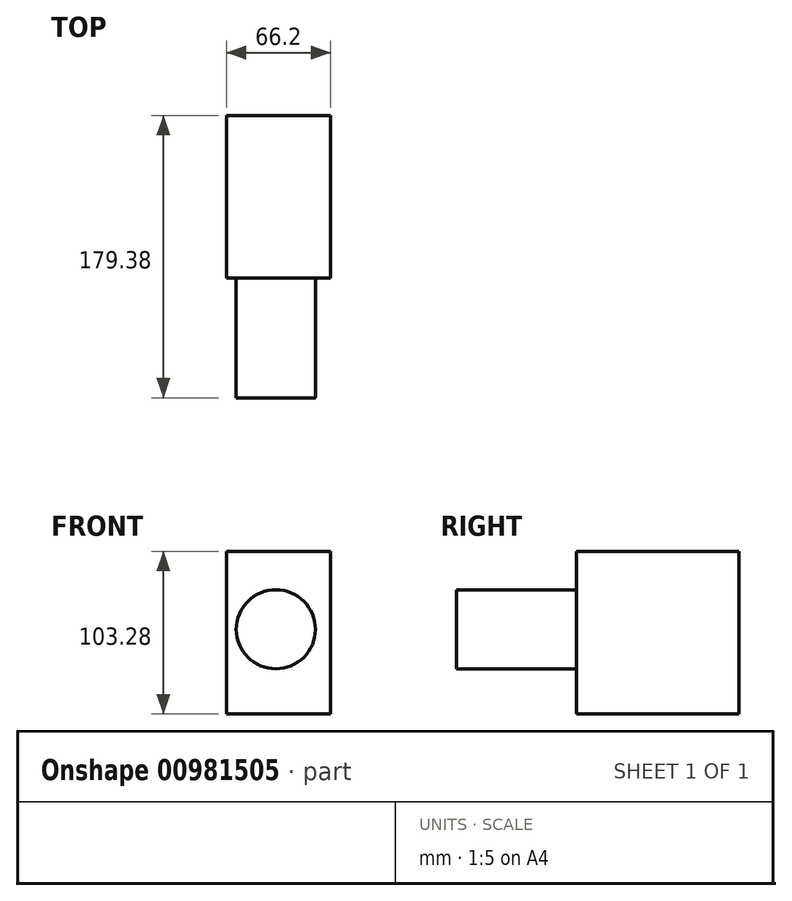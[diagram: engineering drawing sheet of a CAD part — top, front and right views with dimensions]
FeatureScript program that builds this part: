
annotation { "Feature Type Name" : "Feature", "Feature Type Description" : "" }
export const myFeature = defineFeature(function(context is Context, id is Id, definition is map)
    precondition{}
    {
        {
            var Q0;
            Q0=qCreatedBy(makeId("Top.planeOp"),FACE);
            var sketch = newSketch(context, id + "F0", { "sketchPlane" : qUnion([Q0])});
            skLineSegment(sketch, "E0.bottom", {"start": v(17.44, -38.98) * mm, "end": v(-48.76, -38.98) * mm});
            skLineSegment(sketch, "E0.top", {"start": v(17.44, 64.3) * mm, "end": v(-48.76, 64.3) * mm});
            skLineSegment(sketch, "E0.left", {"start": v(17.44, -38.98) * mm, "end": v(17.44, 64.3) * mm});
            skLineSegment(sketch, "E0.right", {"start": v(-48.76, -38.98) * mm, "end": v(-48.76, 64.3) * mm});
            skSolve(sketch);
        }
        {
            var Q0;
            Q0=makeQuery(id+"F0.imprint","IMPRINT",FACE,{"disambiguationData":[TD([[makeQuery(id+"F0.imprint","IMPRINT",EDGE,{"derivedFrom":sQuery(id+"F0.wireOp",EDGE,"E0.bottom")}),-1.0]])]});
            extrude(context, id + "F1", {"entities" : qUnion([Q0]), "depth" : 103.28 * mm, "offsetDistance" : 25.4 * mm});
        }
        {
            var Q0;
            Q0=makeQuery(id+"F1.opExtrude","SWEPT_FACE",FACE,{"disambiguationData":[OSD([sQuery(id+"F0.wireOp",EDGE,"E0.bottom")])]});
            var sketch = newSketch(context, id + "F2", { "sketchPlane" : qUnion([Q0])});
            skCircle(sketch, "E1", {"center": v(-17.36, 53.8) * mm, "radius": 25.13 * mm});
            skSolve(sketch);
        }
        {
            var Q0;
            Q0 = qSketchRegion(id + "F2", true);
            var sketch = newSketch(context, id + "F3", { "sketchPlane" : qUnion([Q0])});
            skSolve(sketch);
        }
        {
            var Q0;
            Q0=makeQuery(id+"F3.imprint","IMPRINT",FACE,{"disambiguationData":[TD([[makeQuery(id+"F3.imprint","IMPRINT",EDGE,{"derivedFrom":makeQuery(id+"F2.imprint","IMPRINT",EDGE,{"derivedFrom":sQuery(id+"F2.wireOp",EDGE,"E1")})}),1.0]])]});
            extrude(context, id + "F4", {"entities" : qUnion([Q0]), "operationType" : NewBodyOperationType.ADD, "depth" : 76.1 * mm, "offsetDistance" : 25.4 * mm});
        }
    });
